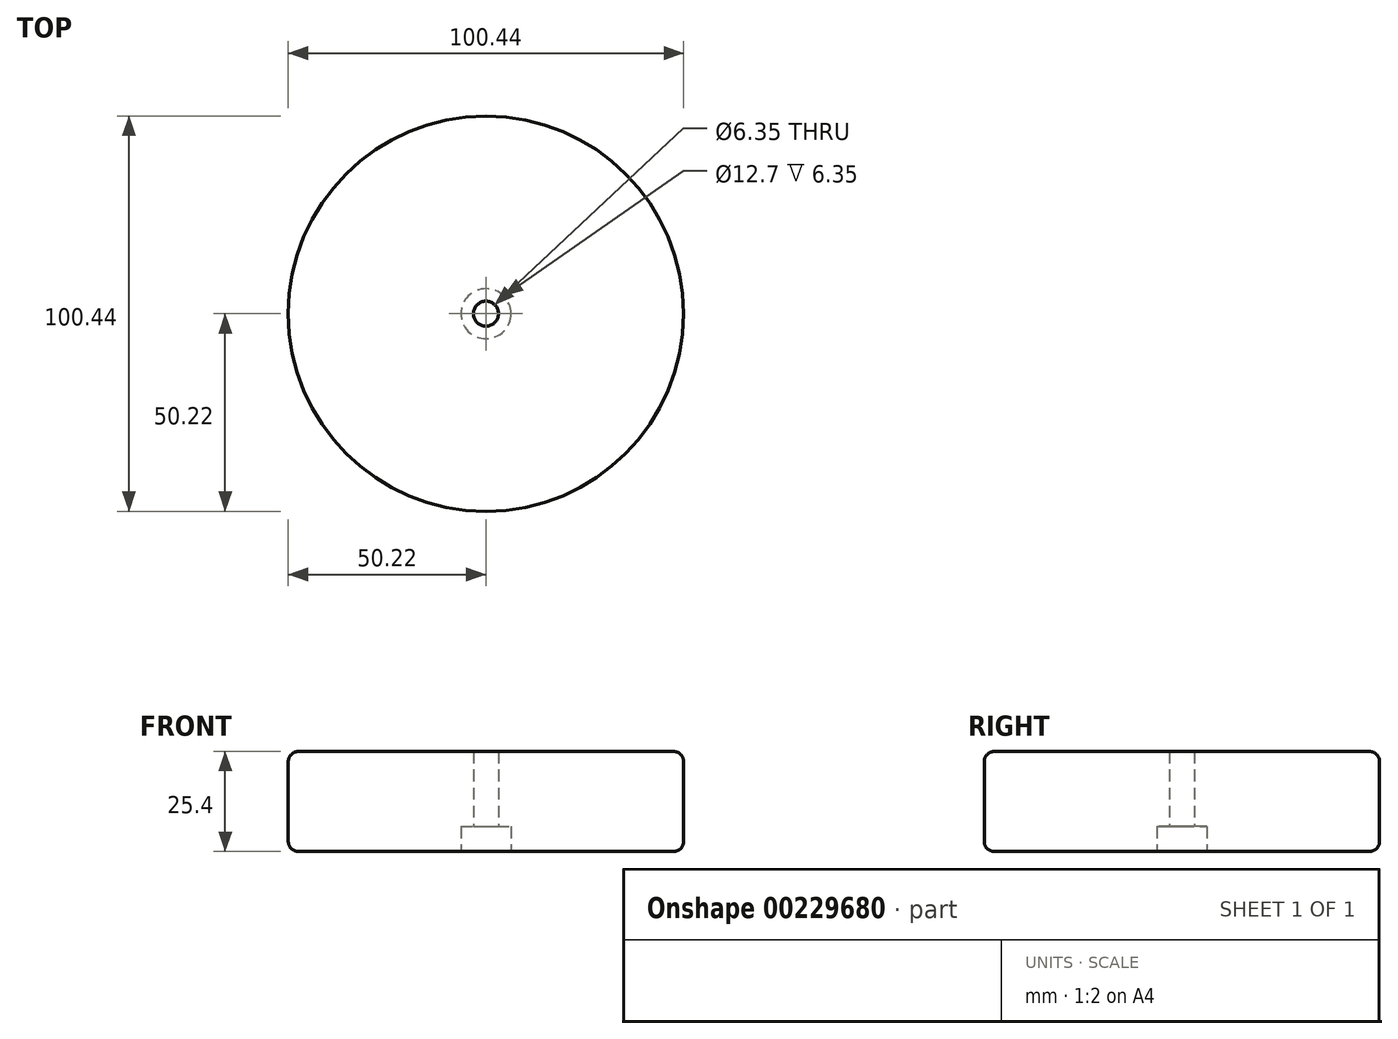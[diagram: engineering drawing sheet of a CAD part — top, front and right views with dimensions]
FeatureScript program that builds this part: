
annotation { "Feature Type Name" : "Feature", "Feature Type Description" : "" }
export const myFeature = defineFeature(function(context is Context, id is Id, definition is map)
    precondition{}
    {
        {
            var Q0;
            Q0=qCreatedBy(makeId("Top.planeOp"),FACE);
            var sketch = newSketch(context, id + "F0", { "sketchPlane" : qUnion([Q0])});
            skCircle(sketch, "E0", {"center": v(0, 0) * mm, "radius": 50.22 * mm});
            skSolve(sketch);
        }
        {
            var Q0;
            Q0=makeQuery(id+"F0.imprint","IMPRINT",FACE,{"disambiguationData":[TD([[makeQuery(id+"F0.imprint","IMPRINT",EDGE,{"derivedFrom":sQuery(id+"F0.wireOp",EDGE,"E0")}),1.0]])]});
            extrude(context, id + "F1", {"entities" : qUnion([Q0]), "depth" : 25.4 * mm});
        }
        {
            var Q0;
            Q0=makeQuery(id+"F1.opExtrude","CAP_EDGE",EDGE,{"disambiguationData":[OSD([sQuery(id+"F0.wireOp",EDGE,"E0")])],"isStart":false});
            fillet(context, id + "F2", {"entities" : qUnion([Q0]), "radius" : 2.54 * mm, "tangentPropagation" : true, "allowEdgeOverflow" : false});
        }
        {
            var Q0;
            Q0=makeQuery(id+"F1.opExtrude","CAP_EDGE",EDGE,{"disambiguationData":[OSD([sQuery(id+"F0.wireOp",EDGE,"E0")])],"isStart":true});
            fillet(context, id + "F3", {"entities" : qUnion([Q0]), "radius" : 2.54 * mm, "tangentPropagation" : true, "allowEdgeOverflow" : false});
        }
        {
            var Q0;
            Q0=sQuery(id+"F0.wireOp",VERTEX,"E0.center");
            var Q1;
            Q1=makeQuery(id+"F1.opExtrude","SWEPT_BODY",BODY,{"disambiguationData":[OSD([sQuery(id+"F0.wireOp",EDGE,"E0")])]});
            hole(context, id + "F4", {"style" : HoleStyle.C_BORE, "endStyle" : HoleEndStyle.THROUGH, "oppositeDirection" : true, "holeDiameter" : 6.35 * mm, "cBoreDiameter" : 12.7 * mm, "cBoreDepth" : 6.35 * mm, "locations" : qUnion([Q0]), "scope" : qUnion([Q1]), "isTappedThrough" : true});
        }
    });
